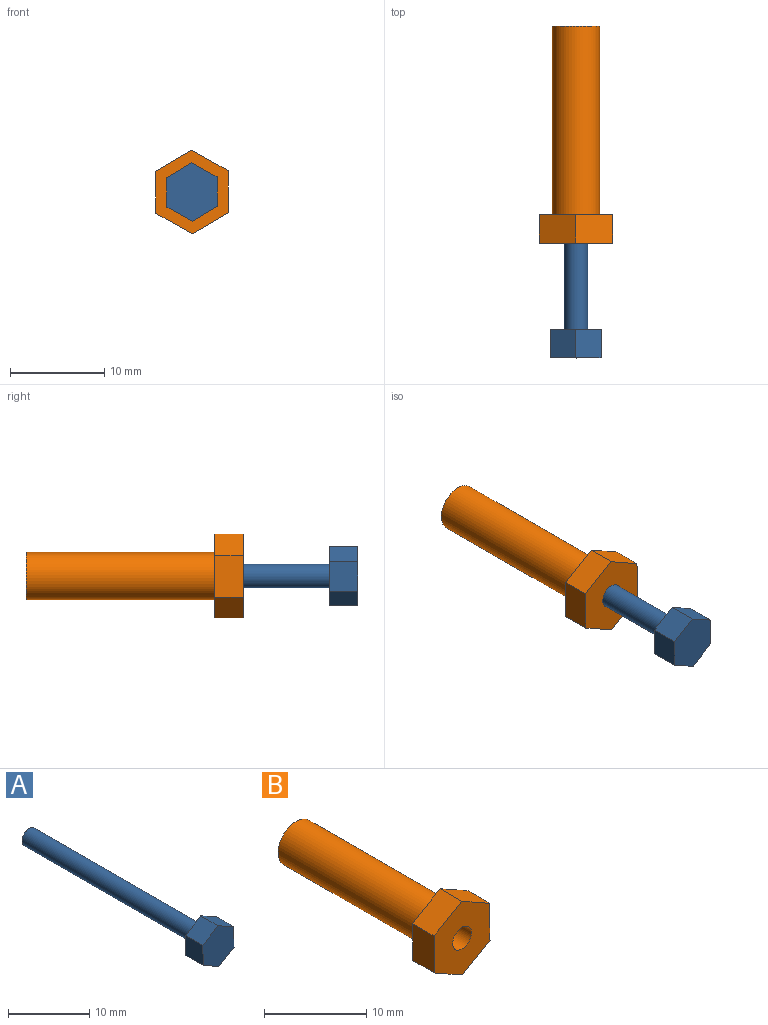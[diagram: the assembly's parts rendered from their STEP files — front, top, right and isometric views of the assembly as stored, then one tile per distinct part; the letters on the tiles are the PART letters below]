
ASSEMBLY  parts=2 mates=1
PART A: 10 faces, bbox 5.4x33x6.2 mm
  f0: cylinder r=1.25mm len=30mm, axis (0,1,0), area 235.6mm2, adj f1,f9
  f1: plane 2.5x2.5mm, normal (0,1,0), area 4.9mm2, adj f0
  f2: plane 3x2.65mm, normal (-0.52,0,0.86), area 9.3mm2, adj f3,f7,f8,f9
  f3: plane 3.1x3mm, normal (-1,0,-0.02), area 9.3mm2, adj f2,f4,f8,f9
  f4: plane 3x2.72mm, normal (-0.48,0,-0.88), area 9.3mm2, adj f3,f5,f8,f9
  f5: plane 3x2.65mm, normal (0.52,0,-0.86), area 9.3mm2, adj f4,f6,f8,f9
  f6: plane 3.1x3mm, normal (1,0,0.02), area 9.3mm2, adj f5,f7,f8,f9
  f7: plane 3x2.72mm, normal (0.48,0,0.88), area 9.3mm2, adj f2,f6,f8,f9
  f8: plane 6.2x5.43mm, normal (0,-1,0), area 25mm2, adj f2,f3,f4,f5,f6,f7
  f9: plane 6.2x5.43mm, normal (0,1,0), area 20.1mm2, adj f0,f2,f3,f4,f5,f6,f7
PART B: 11 faces, bbox 7.7x23x8.9 mm
  f0: cylinder r=1.3mm len=23mm, axis (0,1,0), area 187.9mm2, adj f2,f9
  f1: cylinder r=2.5mm len=20mm, axis (0,1,0), area 314.2mm2, adj f2,f10
  f2: plane 5x5mm, normal (0,1,0), area 14.3mm2, adj f0,f1
  f3: plane 3.83x3mm, normal (-0.51,0,0.86), area 13.3mm2, adj f4,f8,f9,f10
  f4: plane 4.45x3mm, normal (-1,0,-0.01), area 13.3mm2, adj f3,f5,f9,f10
  f5: plane 3.87x3mm, normal (-0.49,0,-0.87), area 13.3mm2, adj f4,f6,f9,f10
  f6: plane 3.83x3mm, normal (0.51,0,-0.86), area 13.3mm2, adj f5,f7,f9,f10
  f7: plane 4.45x3mm, normal (1,0,0.01), area 13.3mm2, adj f6,f8,f9,f10
  f8: plane 3.87x3mm, normal (0.49,0,0.87), area 13.3mm2, adj f3,f7,f9,f10
  f9: plane 8.89x7.75mm, normal (0,-1,0), area 46.1mm2, adj f0,f3,f4,f5,f6,f7,f8
  f10: plane 8.89x7.75mm, normal (0,1,0), area 31.7mm2, adj f1,f3,f4,f5,f6,f7,f8
PLACE A t=(0.18,-5.96,6.64)mm
PLACE B t=(0.18,-3.79,6.64)mm
MATE slider A.f0 <-> B.f1  axis (0,1,0) through (0.18,-5.96,6.64)mm
